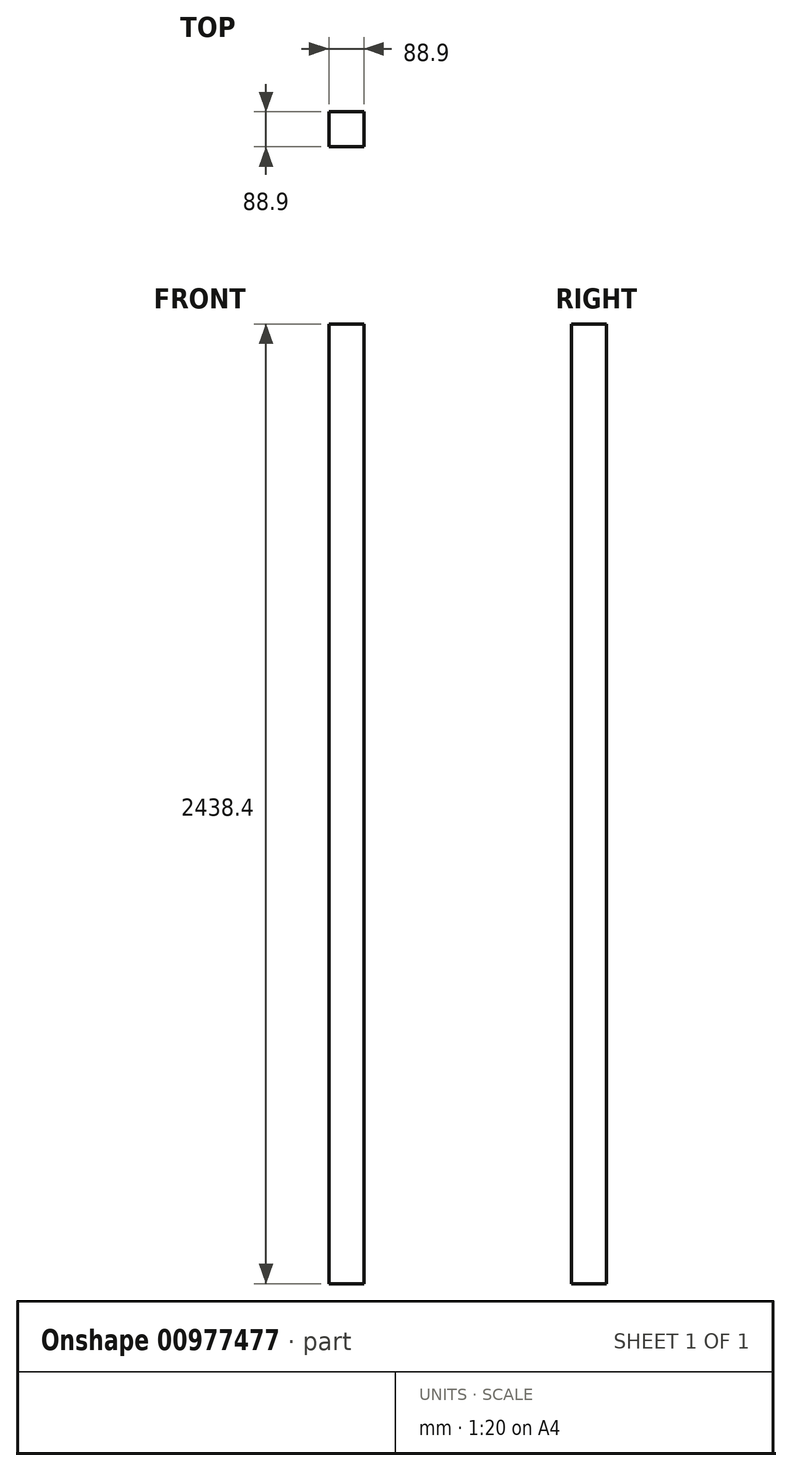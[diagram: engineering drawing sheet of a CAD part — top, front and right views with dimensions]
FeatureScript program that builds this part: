
annotation { "Feature Type Name" : "Feature", "Feature Type Description" : "" }
export const myFeature = defineFeature(function(context is Context, id is Id, definition is map)
    precondition{}
    {
        {
            var Q0;
            Q0=qCreatedBy(makeId("Top.planeOp"),FACE);
            var sketch = newSketch(context, id + "F0", { "sketchPlane" : qUnion([Q0])});
            skLineSegment(sketch, "E0.bottom", {"start": v(0, 0) * mm, "end": v(88.9, 0) * mm});
            skLineSegment(sketch, "E0.top", {"start": v(0, 88.9) * mm, "end": v(88.9, 88.9) * mm});
            skLineSegment(sketch, "E0.left", {"start": v(0, 0) * mm, "end": v(0, 88.9) * mm});
            skLineSegment(sketch, "E0.right", {"start": v(88.9, 0) * mm, "end": v(88.9, 88.9) * mm});
            skSolve(sketch);
        }
        {
            var Q0;
            Q0 = qSketchRegion(id + "F0", true);
            extrude(context, id + "F1", {"entities" : qUnion([Q0]), "depth" : 2438.4 * mm, "offsetDistance" : 25.4 * mm});
        }
    });
